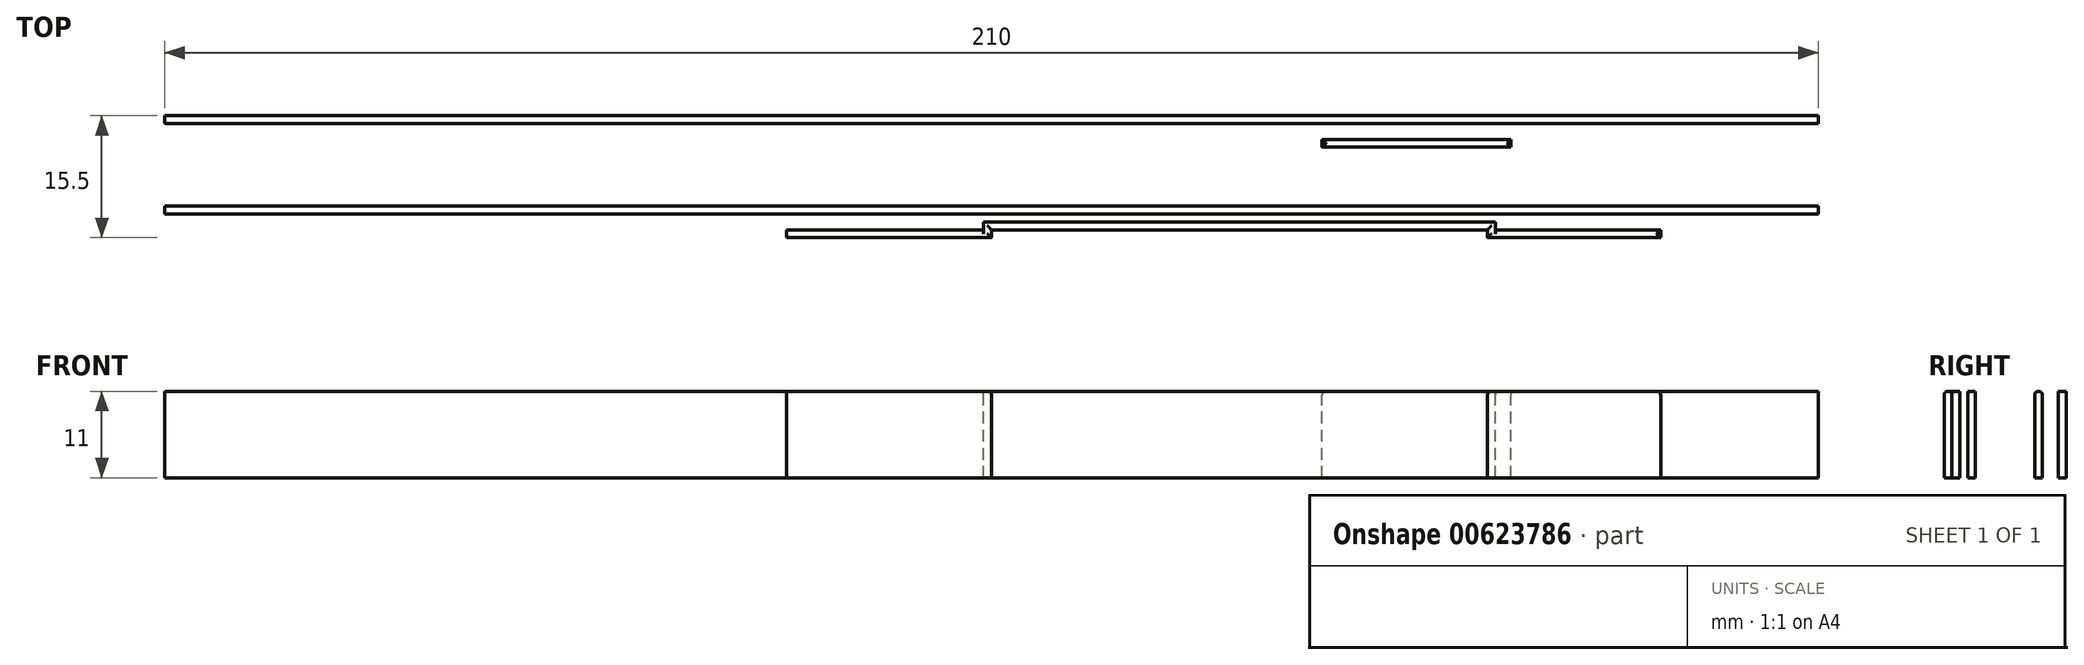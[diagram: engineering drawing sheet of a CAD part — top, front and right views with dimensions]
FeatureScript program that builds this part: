
annotation { "Feature Type Name" : "Feature", "Feature Type Description" : "" }
export const myFeature = defineFeature(function(context is Context, id is Id, definition is map)
    precondition{}
    {
        {
            var Q0;
            Q0=qCreatedBy(makeId("Top.planeOp"),FACE);
            var sketch = newSketch(context, id + "F0", { "sketchPlane" : qUnion([Q0])});
            skLineSegment(sketch, "E0.bottom", {"start": v(-105, 1.5) * mm, "end": v(105, 1.5) * mm});
            skLineSegment(sketch, "E0.top", {"start": v(-105, -1.5) * mm, "end": v(105, -1.5) * mm});
            skLineSegment(sketch, "E0.left", {"start": v(-105, 1.5) * mm, "end": v(-105, -1.5) * mm});
            skLineSegment(sketch, "E0.right", {"start": v(105, 1.5) * mm, "end": v(105, -1.5) * mm});
            skPoint(sketch, "E0.middle", {"position": v(0, 0) * mm});
            skLineSegment(sketch, "E1.top", {"start": v(-105, 0.5) * mm, "end": v(105, 0.5) * mm});
            skLineSegment(sketch, "E1.left", {"start": v(-105, 1.5) * mm, "end": v(-105, 0.5) * mm});
            skLineSegment(sketch, "E1.right", {"start": v(105, 1.5) * mm, "end": v(105, 0.5) * mm});
            skLineSegment(sketch, "E2.top", {"start": v(-105, -0.5) * mm, "end": v(105, -0.5) * mm});
            skLineSegment(sketch, "E2.left", {"start": v(-105, -1.5) * mm, "end": v(-105, -0.5) * mm});
            skLineSegment(sketch, "E2.right", {"start": v(105, -1.5) * mm, "end": v(105, -0.5) * mm});
            skLineSegment(sketch, "E3.bottom", {"start": v(43, -1.5) * mm, "end": v(65, -1.5) * mm});
            skLineSegment(sketch, "E3.top", {"start": v(43, -2.5) * mm, "end": v(65, -2.5) * mm});
            skLineSegment(sketch, "E3.left", {"start": v(43, -1.5) * mm, "end": v(43, -2.5) * mm});
            skLineSegment(sketch, "E3.right", {"start": v(65, -1.5) * mm, "end": v(65, -2.5) * mm});
            skLineSegment(sketch, "E4", {"start": v(-105, -1.5) * mm, "end": v(43, -1.5) * mm, "construction": true});
            skLineSegment(sketch, "E5.top", {"start": v(43, -0.5) * mm, "end": v(65, -0.5) * mm});
            skLineSegment(sketch, "E5.left", {"start": v(43, -1.5) * mm, "end": v(43, -0.5) * mm});
            skLineSegment(sketch, "E5.right", {"start": v(65, -1.5) * mm, "end": v(65, -0.5) * mm});
            skLineSegment(sketch, "E6.bottom", {"start": v(43, -2.5) * mm, "end": v(42, -2.5) * mm});
            skLineSegment(sketch, "E6.top", {"start": v(43, -1.5) * mm, "end": v(42, -1.5) * mm});
            skLineSegment(sketch, "E6.left", {"start": v(43, -2.5) * mm, "end": v(43, -1.5) * mm});
            skLineSegment(sketch, "E6.right", {"start": v(42, -2.5) * mm, "end": v(42, -1.5) * mm});
            skLineSegment(sketch, "E7.bottom", {"start": v(65, -2.5) * mm, "end": v(66, -2.5) * mm});
            skLineSegment(sketch, "E7.top", {"start": v(65, -1.5) * mm, "end": v(66, -1.5) * mm});
            skLineSegment(sketch, "E7.left", {"start": v(65, -2.5) * mm, "end": v(65, -1.5) * mm});
            skLineSegment(sketch, "E7.right", {"start": v(66, -2.5) * mm, "end": v(66, -1.5) * mm});
            skSolve(sketch);
        }
        {
            var Q0;
            Q0=qCreatedBy(makeId("Top.planeOp"),FACE);
            var sketch = newSketch(context, id + "F1", { "sketchPlane" : qUnion([Q0])});
            skLineSegment(sketch, "E8.bottom", {"start": v(-105, -10) * mm, "end": v(105, -10) * mm});
            skLineSegment(sketch, "E8.top", {"start": v(-105, -13) * mm, "end": v(105, -13) * mm});
            skLineSegment(sketch, "E8.left", {"start": v(-105, -10) * mm, "end": v(-105, -13) * mm});
            skLineSegment(sketch, "E8.right", {"start": v(105, -10) * mm, "end": v(105, -13) * mm});
            skLineSegment(sketch, "E9", {"start": v(0, 0) * mm, "end": v(0, -10) * mm, "construction": true});
            skLineSegment(sketch, "E10", {"start": v(-105, -10) * mm, "end": v(0, -10) * mm, "construction": true});
            skLineSegment(sketch, "E11.top", {"start": v(-105, -11) * mm, "end": v(105, -11) * mm});
            skLineSegment(sketch, "E11.left", {"start": v(-105, -10) * mm, "end": v(-105, -11) * mm});
            skLineSegment(sketch, "E11.right", {"start": v(105, -10) * mm, "end": v(105, -11) * mm});
            skLineSegment(sketch, "E12.top", {"start": v(-105, -12) * mm, "end": v(105, -12) * mm});
            skLineSegment(sketch, "E12.left", {"start": v(-105, -13) * mm, "end": v(-105, -12) * mm});
            skLineSegment(sketch, "E12.right", {"start": v(105, -13) * mm, "end": v(105, -12) * mm});
            skLineSegment(sketch, "E13", {"start": v(-105, -13) * mm, "end": v(-26, -13) * mm, "construction": true});
            skLineSegment(sketch, "E14.bottom", {"start": v(-26, -13) * mm, "end": v(0, -13) * mm});
            skLineSegment(sketch, "E14.top", {"start": v(-26, -14) * mm, "end": v(0, -14) * mm});
            skLineSegment(sketch, "E14.left", {"start": v(-26, -13) * mm, "end": v(-26, -14) * mm});
            skLineSegment(sketch, "E14.right", {"start": v(0, -13) * mm, "end": v(0, -14) * mm});
            skLineSegment(sketch, "E15.bottom", {"start": v(-25, -13) * mm, "end": v(-1, -13) * mm});
            skLineSegment(sketch, "E15.top", {"start": v(-25, -12) * mm, "end": v(-1, -12) * mm});
            skLineSegment(sketch, "E15.left", {"start": v(-25, -13) * mm, "end": v(-25, -12) * mm});
            skLineSegment(sketch, "E15.right", {"start": v(-1, -13) * mm, "end": v(-1, -12) * mm});
            skLineSegment(sketch, "E16", {"start": v(-26, -13) * mm, "end": v(-25, -13) * mm, "construction": true});
            skLineSegment(sketch, "E17.bottom", {"start": v(64, -12) * mm, "end": v(84, -12) * mm});
            skLineSegment(sketch, "E17.top", {"start": v(64, -13) * mm, "end": v(84, -13) * mm});
            skLineSegment(sketch, "E17.left", {"start": v(64, -12) * mm, "end": v(64, -13) * mm});
            skLineSegment(sketch, "E17.right", {"start": v(84, -12) * mm, "end": v(84, -13) * mm});
            skLineSegment(sketch, "E18", {"start": v(-1, -12) * mm, "end": v(64, -12) * mm, "construction": true});
            skLineSegment(sketch, "E19.bottom", {"start": v(63, -13) * mm, "end": v(85, -13) * mm});
            skLineSegment(sketch, "E19.top", {"start": v(63, -14) * mm, "end": v(85, -14) * mm});
            skLineSegment(sketch, "E19.left", {"start": v(63, -13) * mm, "end": v(63, -14) * mm});
            skLineSegment(sketch, "E19.right", {"start": v(85, -13) * mm, "end": v(85, -14) * mm});
            skLineSegment(sketch, "E20", {"start": v(63, -13) * mm, "end": v(64, -13) * mm, "construction": true});
            skSolve(sketch);
        }
        {
            var Q0;
            {var subQ1=sQuery(id+"F1.wireOp",EDGE,"E8.left");Q0=makeQuery(id+"F1.imprint","IMPRINT",FACE,{"disambiguationData":[TD([[makeQuery(id+"F1.imprint","IMPRINT",EDGE,{"derivedFrom":subQ1}),1.0]])]});}
            var Q1;
            Q1=makeQuery(id+"F1.imprint","IMPRINT",FACE,{"disambiguationData":[TD([[makeQuery(id+"F1.imprint","IMPRINT",EDGE,{"derivedFrom":sQuery(id+"F1.wireOp",EDGE,"E17.bottom")}),-1.0]])]});
            var Q2;
            Q2=makeQuery(id+"F1.imprint","IMPRINT",FACE,{"disambiguationData":[TD([[makeQuery(id+"F1.imprint","IMPRINT",EDGE,{"derivedFrom":sQuery(id+"F1.wireOp",EDGE,"E15.bottom")}),1.0]])]});
            extrude(context, id + "F2", {"entities" : qUnion([Q0, Q1, Q2]), "oppositeDirection" : true, "depth" : 1 * mm, "offsetDistance" : 25 * mm});
        }
        {
            var Q0;
            Q0=makeQuery(id+"F1.imprint","IMPRINT",FACE,{"disambiguationData":[TD([[makeQuery(id+"F1.imprint","IMPRINT",EDGE,{"derivedFrom":sQuery(id+"F1.wireOp",EDGE,"E8.bottom")}),-1.0]])]});
            var Q1;
            Q1=makeQuery(id+"F1.imprint","IMPRINT",FACE,{"disambiguationData":[TD([[makeQuery(id+"F1.imprint","IMPRINT",EDGE,{"derivedFrom":sQuery(id+"F1.wireOp",EDGE,"E14.top")}),1.0]])]});
            var Q2;
            {var subQ0=sQuery(id+"F1.wireOp",EDGE,"E12.left");Q2=makeQuery(id+"F1.imprint","IMPRINT",FACE,{"disambiguationData":[TD([[makeQuery(id+"F1.imprint","IMPRINT",EDGE,{"derivedFrom":subQ0}),-1.0]])]});}
            var Q3;
            {var subQ3=sQuery(id+"F1.wireOp",EDGE,"E15.right");Q3=makeQuery(id+"F1.imprint","IMPRINT",FACE,{"disambiguationData":[TD([[makeQuery(id+"F1.imprint","IMPRINT",EDGE,{"derivedFrom":subQ3}),-1.0]])]});}
            var Q4;
            Q4=makeQuery(id+"F1.imprint","IMPRINT",FACE,{"disambiguationData":[TD([[makeQuery(id+"F1.imprint","IMPRINT",EDGE,{"derivedFrom":sQuery(id+"F1.wireOp",EDGE,"E19.top")}),1.0]])]});
            var Q5;
            {var subQ1=sQuery(id+"F1.wireOp",EDGE,"E12.right");Q5=makeQuery(id+"F1.imprint","IMPRINT",FACE,{"disambiguationData":[TD([[makeQuery(id+"F1.imprint","IMPRINT",EDGE,{"derivedFrom":subQ1}),1.0]])]});}
            extrude(context, id + "F3", {"entities" : qUnion([Q0, Q1, Q2, Q3, Q4, Q5]), "operationType" : NewBodyOperationType.ADD, "oppositeDirection" : true, "depth" : 11 * mm, "offsetDistance" : 25 * mm});
        }
        {
            var Q0;
            {var subQ1=sQuery(id+"F0.wireOp",EDGE,"E0.left");Q0=makeQuery(id+"F0.imprint","IMPRINT",FACE,{"disambiguationData":[TD([[makeQuery(id+"F0.imprint","IMPRINT",EDGE,{"derivedFrom":subQ1}),1.0]])]});}
            var Q1;
            Q1=makeQuery(id+"F0.imprint","IMPRINT",FACE,{"disambiguationData":[TD([[makeQuery(id+"F0.imprint","IMPRINT",EDGE,{"derivedFrom":sQuery(id+"F0.wireOp",EDGE,"E3.bottom")}),1.0]])]});
            extrude(context, id + "F4", {"entities" : qUnion([Q0, Q1]), "oppositeDirection" : true, "depth" : 1 * mm, "offsetDistance" : 25 * mm});
        }
        {
            var Q0;
            Q0=makeQuery(id+"F0.imprint","IMPRINT",FACE,{"disambiguationData":[TD([[makeQuery(id+"F0.imprint","IMPRINT",EDGE,{"derivedFrom":sQuery(id+"F0.wireOp",EDGE,"E3.top")}),1.0]])]});
            var Q1;
            Q1=makeQuery(id+"F0.imprint","IMPRINT",FACE,{"disambiguationData":[TD([[makeQuery(id+"F0.imprint","IMPRINT",EDGE,{"derivedFrom":sQuery(id+"F0.wireOp",EDGE,"E6.bottom")}),-1.0]])]});
            var Q2;
            {var subQ1=sQuery(id+"F0.wireOp",EDGE,"E2.left");Q2=makeQuery(id+"F0.imprint","IMPRINT",FACE,{"disambiguationData":[TD([[makeQuery(id+"F0.imprint","IMPRINT",EDGE,{"derivedFrom":subQ1}),-1.0]])]});}
            var Q3;
            Q3=makeQuery(id+"F0.imprint","IMPRINT",FACE,{"disambiguationData":[TD([[makeQuery(id+"F0.imprint","IMPRINT",EDGE,{"derivedFrom":sQuery(id+"F0.wireOp",EDGE,"E7.bottom")}),1.0]])]});
            var Q4;
            {var subQ1=sQuery(id+"F0.wireOp",EDGE,"E2.right");Q4=makeQuery(id+"F0.imprint","IMPRINT",FACE,{"disambiguationData":[TD([[makeQuery(id+"F0.imprint","IMPRINT",EDGE,{"derivedFrom":subQ1}),1.0]])]});}
            var Q5;
            Q5=makeQuery(id+"F0.imprint","IMPRINT",FACE,{"disambiguationData":[TD([[makeQuery(id+"F0.imprint","IMPRINT",EDGE,{"derivedFrom":sQuery(id+"F0.wireOp",EDGE,"E0.bottom")}),-1.0]])]});
            extrude(context, id + "F5", {"entities" : qUnion([Q0, Q1, Q2, Q3, Q4, Q5]), "operationType" : NewBodyOperationType.ADD, "oppositeDirection" : true, "depth" : 11 * mm, "offsetDistance" : 25 * mm});
        }
        {
            var Q0;
            Q0=makeQuery(id+"F5.opExtrude","CAP_EDGE",EDGE,{"disambiguationData":[OSD([sQuery(id+"F0.wireOp",EDGE,"E0.bottom")])],"isStart":true});
            var Q1;
            {var subQ0=sQuery(id+"F0.wireOp",EDGE,"E0.top");Q1=makeQuery(id+"F5.opExtrude","CAP_EDGE",EDGE,{"disambiguationData":[OSD([subQ0]),TDD([makeQuery(id+"F0.imprint","IMPRINT",EDGE,{"disambiguationData":[TD([[makeQuery(id+"F0.imprint","INTERSECT",VERTEX,{"derivedFrom":[subQ0,sQuery(id+"F0.wireOp",EDGE,"E2.left")]}),-1.0]])],"derivedFrom":subQ0})])],"isStart":true});}
            var Q2;
            Q2=makeQuery(id+"F5.opExtrude","CAP_EDGE",EDGE,{"disambiguationData":[OSD([sQuery(id+"F0.wireOp",EDGE,"E3.top"),sQuery(id+"F0.wireOp",EDGE,"E6.bottom"),sQuery(id+"F0.wireOp",EDGE,"E7.bottom")])],"isStart":true});
            var Q3;
            {var subQ0=sQuery(id+"F0.wireOp",EDGE,"E0.top");Q3=makeQuery(id+"F5.opExtrude","CAP_EDGE",EDGE,{"disambiguationData":[OSD([subQ0]),TDD([makeQuery(id+"F0.imprint","IMPRINT",EDGE,{"disambiguationData":[TD([[makeQuery(id+"F0.imprint","INTERSECT",VERTEX,{"derivedFrom":[subQ0,sQuery(id+"F0.wireOp",EDGE,"E2.right")]}),1.0]])],"derivedFrom":subQ0})])],"isStart":true});}
            var Q4;
            Q4=makeQuery(id+"F5.opExtrude","CAP_EDGE",EDGE,{"disambiguationData":[OSD([sQuery(id+"F0.wireOp",EDGE,"E6.right")])],"isStart":true});
            var Q5;
            Q5=makeQuery(id+"F5.opExtrude","CAP_EDGE",EDGE,{"disambiguationData":[OSD([sQuery(id+"F0.wireOp",EDGE,"E7.right")])],"isStart":true});
            var Q6;
            Q6=makeQuery(id+"F3.opExtrude","CAP_EDGE",EDGE,{"disambiguationData":[OSD([sQuery(id+"F1.wireOp",EDGE,"E8.bottom")])],"isStart":true});
            var Q7;
            {var subQ0=sQuery(id+"F1.wireOp",EDGE,"E8.top");Q7=makeQuery(id+"F3.opExtrude","CAP_EDGE",EDGE,{"disambiguationData":[OSD([subQ0]),TDD([makeQuery(id+"F1.imprint","IMPRINT",EDGE,{"disambiguationData":[TD([[makeQuery(id+"F1.imprint","INTERSECT",VERTEX,{"derivedFrom":[subQ0,sQuery(id+"F1.wireOp",EDGE,"E14.bottom"),sQuery(id+"F1.wireOp",EDGE,"E14.right")]}),-1.0]])],"derivedFrom":subQ0})])],"isStart":true});}
            var Q8;
            Q8=makeQuery(id+"F3.opExtrude","CAP_EDGE",EDGE,{"disambiguationData":[OSD([sQuery(id+"F1.wireOp",EDGE,"E14.top")])],"isStart":true});
            var Q9;
            Q9=makeQuery(id+"F3.opExtrude","CAP_EDGE",EDGE,{"disambiguationData":[OSD([sQuery(id+"F1.wireOp",EDGE,"E14.right")])],"isStart":true});
            var Q10;
            Q10=makeQuery(id+"F3.opExtrude","CAP_EDGE",EDGE,{"disambiguationData":[OSD([sQuery(id+"F1.wireOp",EDGE,"E19.left")])],"isStart":true});
            var Q11;
            Q11=makeQuery(id+"F3.opExtrude","CAP_EDGE",EDGE,{"disambiguationData":[OSD([sQuery(id+"F1.wireOp",EDGE,"E19.top")])],"isStart":true});
            var Q12;
            Q12=makeQuery(id+"F3.opExtrude","CAP_EDGE",EDGE,{"disambiguationData":[OSD([sQuery(id+"F1.wireOp",EDGE,"E19.right")])],"isStart":true});
            var Q13;
            {var subQ0=sQuery(id+"F1.wireOp",EDGE,"E8.top");Q13=makeQuery(id+"F3.opExtrude","CAP_EDGE",EDGE,{"disambiguationData":[OSD([subQ0]),TDD([makeQuery(id+"F1.imprint","IMPRINT",EDGE,{"disambiguationData":[TD([[makeQuery(id+"F1.imprint","INTERSECT",VERTEX,{"derivedFrom":[subQ0,sQuery(id+"F1.wireOp",EDGE,"E12.right")]}),1.0]])],"derivedFrom":subQ0})])],"isStart":true});}
            var Q14;
            {var subQ0=sQuery(id+"F1.wireOp",EDGE,"E8.top");Q14=makeQuery(id+"F3.opExtrude","CAP_EDGE",EDGE,{"disambiguationData":[OSD([subQ0]),TDD([makeQuery(id+"F1.imprint","IMPRINT",EDGE,{"disambiguationData":[TD([[makeQuery(id+"F1.imprint","INTERSECT",VERTEX,{"derivedFrom":[subQ0,sQuery(id+"F1.wireOp",EDGE,"E12.left")]}),-1.0]])],"derivedFrom":subQ0})])],"isStart":true});}
            fillet(context, id + "F6", {"entities" : qUnion([Q0, Q1, Q2, Q3, Q4, Q5, Q6, Q7, Q8, Q9, Q10, Q11, Q12, Q13, Q14]), "radius" : .5 * mm, "tangentPropagation" : true, "allowEdgeOverflow" : false});
        }
    });
